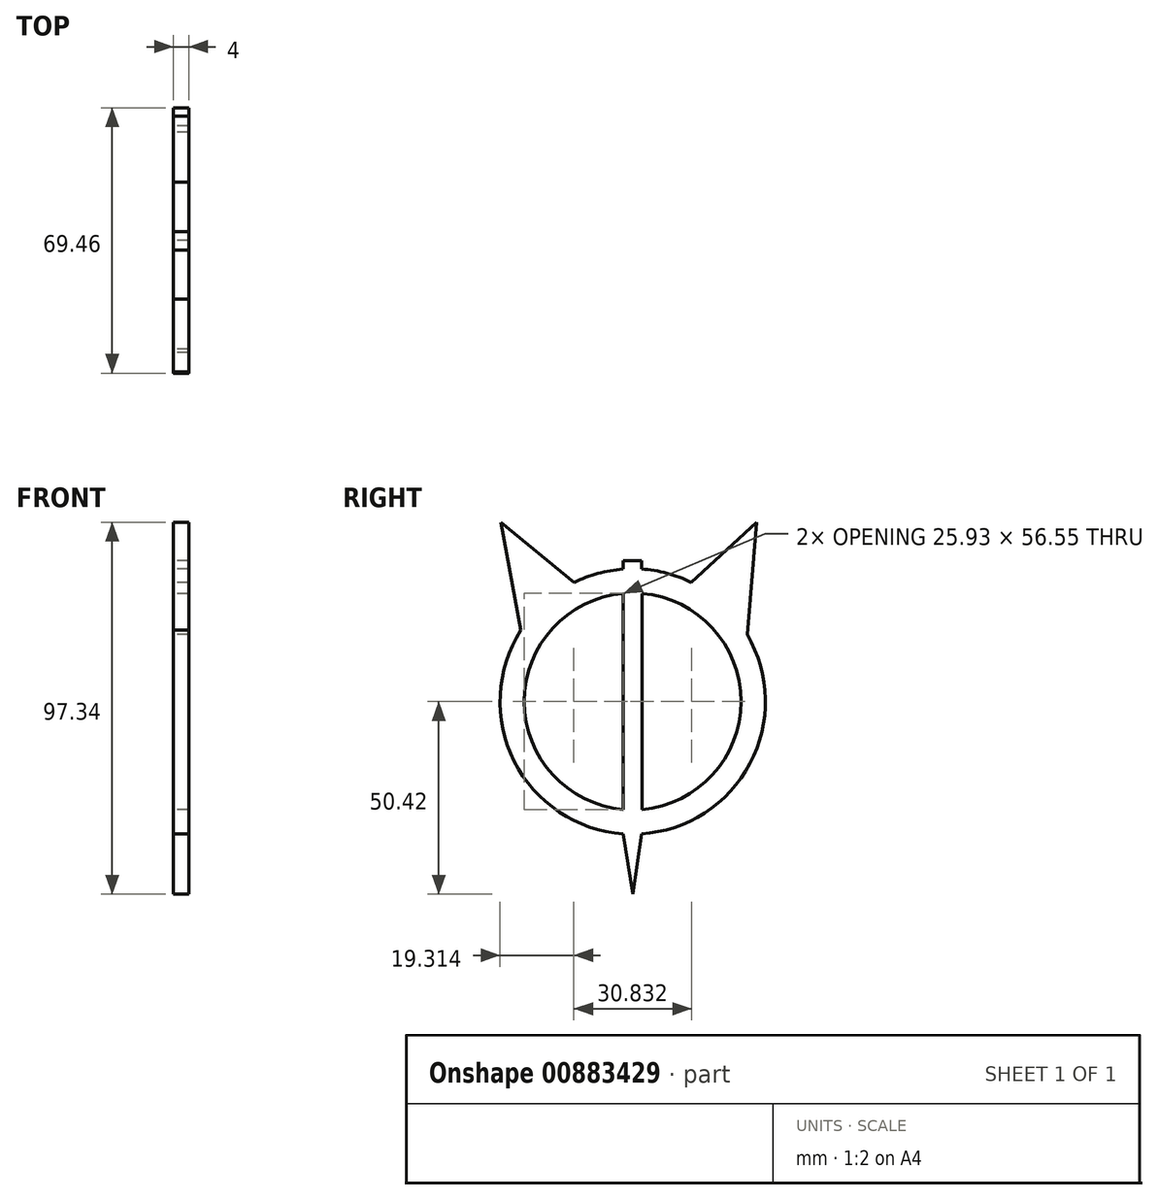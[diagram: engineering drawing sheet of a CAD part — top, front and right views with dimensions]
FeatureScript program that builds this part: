
annotation { "Feature Type Name" : "Feature", "Feature Type Description" : "" }
export const myFeature = defineFeature(function(context is Context, id is Id, definition is map)
    precondition{}
    {
        {
            var Q0;
            Q0=qCreatedBy(makeId("Right.planeOp"),FACE);
            var sketch = newSketch(context, id + "F0", { "sketchPlane" : qUnion([Q0])});
            skArc(sketch, "E0", {"start": v(-2.45, 28.27) * mm, "mid": v(-28.38, 0) * mm, "end": v(-2.45, -28.27) * mm});
            skArc(sketch, "E1", {"start": v(-29.3, 18.64) * mm, "mid": v(-31.03, -15.6) * mm, "end": v(-2.52, -34.64) * mm});
            skLineSegment(sketch, "E2.bottom", {"start": v(-2.45, 28.27) * mm, "end": v(2.45, 28.27) * mm});
            skLineSegment(sketch, "E2.left", {"start": v(-2.45, 28.27) * mm, "end": v(-2.45, -28.27) * mm});
            skLineSegment(sketch, "E2.right", {"start": v(2.45, 28.27) * mm, "end": v(2.45, -28.27) * mm});
            skLineSegment(sketch, "E3", {"start": v(-2.52, -34.64) * mm, "end": v(0, -50.42) * mm});
            skLineSegment(sketch, "E4", {"start": v(0, -50.42) * mm, "end": v(2.27, -34.65) * mm});
            skLineSegment(sketch, "E5", {"start": v(-2.52, 34.64) * mm, "end": v(-2.52, 36.86) * mm});
            skLineSegment(sketch, "E6", {"start": v(-2.52, 36.86) * mm, "end": v(2.27, 36.86) * mm});
            skLineSegment(sketch, "E7", {"start": v(2.27, 36.86) * mm, "end": v(2.27, 34.64) * mm});
            skLineSegment(sketch, "E8", {"start": v(-15.31, 31.17) * mm, "end": v(-34.45, 46.92) * mm});
            skLineSegment(sketch, "E9", {"start": v(-34.45, 46.92) * mm, "end": v(-29.3, 18.64) * mm});
            skLineSegment(sketch, "E10", {"start": v(15.31, 31.17) * mm, "end": v(32.48, 46.92) * mm});
            skLineSegment(sketch, "E11", {"start": v(32.48, 46.92) * mm, "end": v(29.98, 17.53) * mm});
            skArc(sketch, "E12.trimOffspring", {"start": v(15.31, 31.17) * mm, "mid": v(8.96, 33.55) * mm, "end": v(2.27, 34.65) * mm});
            skArc(sketch, "E13.trimOffspring", {"start": v(-2.52, 34.64) * mm, "mid": v(-9.08, 33.52) * mm, "end": v(-15.31, 31.17) * mm});
            skArc(sketch, "E14.trimOffspring", {"start": v(2.45, -28.27) * mm, "mid": v(28.38, 0) * mm, "end": v(2.45, 28.27) * mm});
            skArc(sketch, "E15.trimOffspring", {"start": v(2.27, -34.65) * mm, "mid": v(30.67, -16.29) * mm, "end": v(29.98, 17.53) * mm});
            skLineSegment(sketch, "E16", {"start": v(-2.52, 34.64) * mm, "end": v(2.27, 34.65) * mm});
            skSolve(sketch);
        }
        {
            var Q0;
            Q0=makeQuery(id+"F0.imprint","IMPRINT",FACE,{"disambiguationData":[TD([[makeQuery(id+"F0.imprint","IMPRINT",EDGE,{"derivedFrom":sQuery(id+"F0.wireOp",EDGE,"E0")}),-1.0]])]});
            var Q1;
            Q1=makeQuery(id+"F0.imprint","IMPRINT",FACE,{"disambiguationData":[TD([[makeQuery(id+"F0.imprint","IMPRINT",EDGE,{"derivedFrom":sQuery(id+"F0.wireOp",EDGE,"E5")}),-1.0]])]});
            extrude(context, id + "F1", {"entities" : qUnion([Q0, Q1]), "depth" : 4 * mm, "offsetDistance" : 25 * mm});
        }
    });
